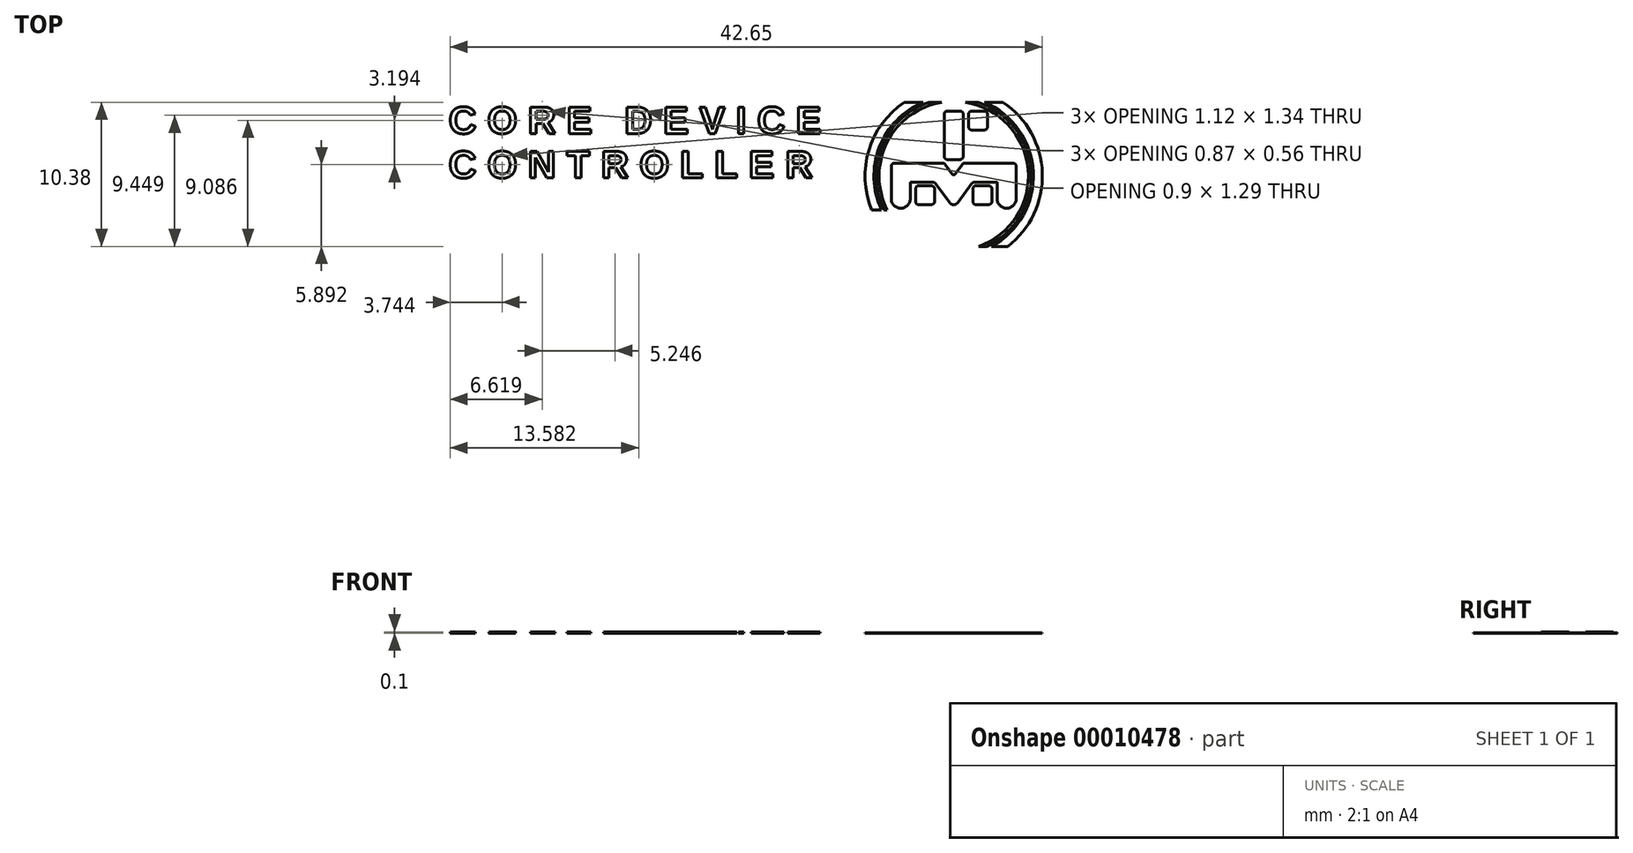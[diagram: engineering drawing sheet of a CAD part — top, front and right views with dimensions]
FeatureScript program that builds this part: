
annotation { "Feature Type Name" : "Feature", "Feature Type Description" : "" }
export const myFeature = defineFeature(function(context is Context, id is Id, definition is map)
    precondition{}
    {
        {
            var Q0;
            Q0=qCreatedBy(makeId("Top.planeOp"),FACE);
            var sketch = newSketch(context, id + "F0", { "sketchPlane" : qUnion([Q0])});
            skLineSegment(sketch, "E0.bottom", {"start": v(62.75, -5.5) * mm, "end": v(66.25, -5.5) * mm});
            skLineSegment(sketch, "E0.top", {"start": v(62.75, -19.5) * mm, "end": v(66.25, -19.5) * mm});
            skLineSegment(sketch, "E0.left", {"start": v(61.75, -6.5) * mm, "end": v(61.75, -18.5) * mm});
            skLineSegment(sketch, "E0.right", {"start": v(67.25, -6.5) * mm, "end": v(67.25, -18.5) * mm});
            skLineSegment(sketch, "E1.bottom", {"start": v(69.75, -5.5) * mm, "end": v(73.25, -5.5) * mm});
            skLineSegment(sketch, "E1.top", {"start": v(69.75, -11) * mm, "end": v(73.25, -11) * mm});
            skLineSegment(sketch, "E1.left", {"start": v(68.75, -6.5) * mm, "end": v(68.75, -10) * mm});
            skLineSegment(sketch, "E1.right", {"start": v(74.25, -6.5) * mm, "end": v(74.25, -10) * mm});
            skLineSegment(sketch, "E2", {"start": v(64.5, -19.5) * mm, "end": v(64.5, -33.5) * mm, "construction": true});
            skLineSegment(sketch, "E3", {"start": v(63.3, -31.86) * mm, "end": v(59.27, -26.4) * mm});
            skLineSegment(sketch, "E4", {"start": v(58.47, -26) * mm, "end": v(52.1, -26) * mm});
            skLineSegment(sketch, "E5", {"start": v(52, -26.1) * mm, "end": v(52, -30.75) * mm});
            skLineSegment(sketch, "E6.0", {"start": v(46.5, -21.5) * mm, "end": v(46.5, -30.75) * mm});
            skLineSegment(sketch, "E6.1", {"start": v(61.24, -20.5) * mm, "end": v(47.5, -20.5) * mm});
            skLineSegment(sketch, "E6.2", {"start": v(64.1, -23.68) * mm, "end": v(62.05, -20.9) * mm});
            skLineSegment(sketch, "E7", {"start": v(49.25, -33.5) * mm, "end": v(49.25, -33.5) * mm});
            skPoint(sketch, "E8.orphan", {"position": v(52, -33.5) * mm});
            skPoint(sketch, "E9.visualSharp", {"position": v(46.5, -33.5) * mm});
            skArc(sketch, "E9.filletArc", {"start": v(46.5, -30.75) * mm, "mid": v(47.3, -32.7) * mm, "end": v(49.25, -33.5) * mm});
            skArc(sketch, "E10.filletArc", {"start": v(49.25, -33.5) * mm, "mid": v(51.2, -32.7) * mm, "end": v(52, -30.75) * mm});
            skLineSegment(sketch, "E11.right", {"start": v(59, -28) * mm, "end": v(59, -31.5) * mm});
            skLineSegment(sketch, "E11.left", {"start": v(53.5, -28) * mm, "end": v(53.5, -31.5) * mm});
            skLineSegment(sketch, "E11.top", {"start": v(54.5, -32.5) * mm, "end": v(58, -32.5) * mm});
            skLineSegment(sketch, "E11.bottom", {"start": v(54.5, -27) * mm, "end": v(58, -27) * mm});
            skPoint(sketch, "E12.0.MirrorP", {"position": v(77, -33.5) * mm});
            skLineSegment(sketch, "E12.1.MirrorCS", {"start": v(74.5, -27) * mm, "end": v(71, -27) * mm});
            skPoint(sketch, "E12.2.MirrorP", {"position": v(82.5, -33.5) * mm});
            skLineSegment(sketch, "E12.3.MirrorCS", {"start": v(70, -28) * mm, "end": v(70, -31.5) * mm});
            skLineSegment(sketch, "E12.4.MirrorCS", {"start": v(75.5, -28) * mm, "end": v(75.5, -31.5) * mm});
            skLineSegment(sketch, "E12.5.MirrorCS", {"start": v(74.5, -32.5) * mm, "end": v(71, -32.5) * mm});
            skLineSegment(sketch, "E12.6.MirrorCS", {"start": v(70.53, -26) * mm, "end": v(76.9, -26) * mm});
            skLineSegment(sketch, "E12.7.MirrorCS", {"start": v(77, -26.1) * mm, "end": v(77, -30.75) * mm});
            skArc(sketch, "E12.8.MirrorCS", {"start": v(79.75, -33.5) * mm, "mid": v(77.8, -32.7) * mm, "end": v(77, -30.75) * mm});
            skLineSegment(sketch, "E12.9.MirrorCS", {"start": v(79.75, -33.5) * mm, "end": v(79.75, -33.5) * mm});
            skLineSegment(sketch, "E12.10.MirrorCS", {"start": v(67.76, -20.5) * mm, "end": v(81.5, -20.5) * mm});
            skPoint(sketch, "E12.11.MirrorP", {"position": v(77, -33.5) * mm});
            skLineSegment(sketch, "E12.12.MirrorCS", {"start": v(64.9, -23.68) * mm, "end": v(66.95, -20.9) * mm});
            skArc(sketch, "E12.13.MirrorCS", {"start": v(82.5, -30.75) * mm, "mid": v(81.7, -32.7) * mm, "end": v(79.75, -33.5) * mm});
            skLineSegment(sketch, "E12.14.MirrorCS", {"start": v(65.7, -31.86) * mm, "end": v(69.73, -26.4) * mm});
            skLineSegment(sketch, "E12.15.MirrorCS", {"start": v(82.5, -21.5) * mm, "end": v(82.5, -30.75) * mm});
            skPoint(sketch, "E13.visualSharp", {"position": v(68.75, -5.5) * mm});
            skArc(sketch, "E13.filletArc", {"start": v(69.75, -5.5) * mm, "mid": v(69.04, -5.8) * mm, "end": v(68.75, -6.5) * mm});
            skPoint(sketch, "E14.visualSharp", {"position": v(74.25, -5.5) * mm});
            skArc(sketch, "E14.filletArc", {"start": v(74.25, -6.5) * mm, "mid": v(73.96, -5.8) * mm, "end": v(73.25, -5.5) * mm});
            skPoint(sketch, "E15.visualSharp", {"position": v(74.25, -11) * mm});
            skArc(sketch, "E15.filletArc", {"start": v(73.25, -11) * mm, "mid": v(73.96, -10.7) * mm, "end": v(74.25, -10) * mm});
            skPoint(sketch, "E16.visualSharp", {"position": v(68.75, -11) * mm});
            skArc(sketch, "E16.filletArc", {"start": v(68.75, -10) * mm, "mid": v(69.04, -10.7) * mm, "end": v(69.75, -11) * mm});
            skPoint(sketch, "E17.visualSharp", {"position": v(67.25, -5.5) * mm});
            skArc(sketch, "E17.filletArc", {"start": v(67.25, -6.5) * mm, "mid": v(66.96, -5.8) * mm, "end": v(66.25, -5.5) * mm});
            skPoint(sketch, "E18.visualSharp", {"position": v(61.75, -5.5) * mm});
            skArc(sketch, "E18.filletArc", {"start": v(62.75, -5.5) * mm, "mid": v(62.04, -5.8) * mm, "end": v(61.75, -6.5) * mm});
            skPoint(sketch, "E19.visualSharp", {"position": v(61.75, -19.5) * mm});
            skArc(sketch, "E19.filletArc", {"start": v(61.75, -18.5) * mm, "mid": v(62.04, -19.2) * mm, "end": v(62.75, -19.5) * mm});
            skPoint(sketch, "E20.visualSharp", {"position": v(67.25, -19.5) * mm});
            skArc(sketch, "E20.filletArc", {"start": v(66.25, -19.5) * mm, "mid": v(66.96, -19.2) * mm, "end": v(67.25, -18.5) * mm});
            skPoint(sketch, "E21.visualSharp", {"position": v(70, -32.5) * mm});
            skArc(sketch, "E21.filletArc", {"start": v(70, -31.5) * mm, "mid": v(70.3, -32.2) * mm, "end": v(71, -32.5) * mm});
            skPoint(sketch, "E22.visualSharp", {"position": v(75.5, -27) * mm});
            skArc(sketch, "E22.filletArc", {"start": v(75.5, -28) * mm, "mid": v(75.2, -27.3) * mm, "end": v(74.5, -27) * mm});
            skPoint(sketch, "E23.visualSharp", {"position": v(70, -27) * mm});
            skArc(sketch, "E23.filletArc", {"start": v(71, -27) * mm, "mid": v(70.3, -27.3) * mm, "end": v(70, -28) * mm});
            skPoint(sketch, "E24.visualSharp", {"position": v(75.5, -32.5) * mm});
            skArc(sketch, "E24.filletArc", {"start": v(74.5, -32.5) * mm, "mid": v(75.2, -32.2) * mm, "end": v(75.5, -31.5) * mm});
            skPoint(sketch, "E25.visualSharp", {"position": v(59, -32.5) * mm});
            skArc(sketch, "E25.filletArc", {"start": v(58, -32.5) * mm, "mid": v(58.7, -32.2) * mm, "end": v(59, -31.5) * mm});
            skPoint(sketch, "E26.visualSharp", {"position": v(59, -27) * mm});
            skArc(sketch, "E26.filletArc", {"start": v(59, -28) * mm, "mid": v(58.7, -27.3) * mm, "end": v(58, -27) * mm});
            skPoint(sketch, "E27.visualSharp", {"position": v(53.5, -27) * mm});
            skArc(sketch, "E27.filletArc", {"start": v(54.5, -27) * mm, "mid": v(53.8, -27.3) * mm, "end": v(53.5, -28) * mm});
            skPoint(sketch, "E28.visualSharp", {"position": v(53.5, -32.5) * mm});
            skArc(sketch, "E28.filletArc", {"start": v(53.5, -31.5) * mm, "mid": v(53.8, -32.2) * mm, "end": v(54.5, -32.5) * mm});
            skPoint(sketch, "E29.visualSharp", {"position": v(46.5, -20.5) * mm});
            skArc(sketch, "E29.filletArc", {"start": v(47.5, -20.5) * mm, "mid": v(46.8, -20.8) * mm, "end": v(46.5, -21.5) * mm});
            skPoint(sketch, "E30.visualSharp", {"position": v(82.5, -20.5) * mm});
            skArc(sketch, "E30.filletArc", {"start": v(82.5, -21.5) * mm, "mid": v(82.2, -20.8) * mm, "end": v(81.5, -20.5) * mm});
            skPoint(sketch, "E31.visualSharp", {"position": v(61.75, -20.5) * mm});
            skArc(sketch, "E31.filletArc", {"start": v(62.05, -20.9) * mm, "mid": v(61.7, -20.6) * mm, "end": v(61.24, -20.5) * mm});
            skPoint(sketch, "E32.visualSharp", {"position": v(67.25, -20.5) * mm});
            skArc(sketch, "E32.filletArc", {"start": v(67.76, -20.5) * mm, "mid": v(67.3, -20.6) * mm, "end": v(66.95, -20.9) * mm});
            skPoint(sketch, "E33.visualSharp", {"position": v(52, -26) * mm});
            skArc(sketch, "E33.filletArc", {"start": v(52.1, -26) * mm, "mid": v(52.03, -26.03) * mm, "end": v(52, -26.1) * mm});
            skPoint(sketch, "E34.visualSharp", {"position": v(77, -26) * mm});
            skArc(sketch, "E34.filletArc", {"start": v(77, -26.1) * mm, "mid": v(76.97, -26.03) * mm, "end": v(76.9, -26) * mm});
            skPoint(sketch, "E35.visualSharp", {"position": v(70.03, -26) * mm});
            skArc(sketch, "E35.filletArc", {"start": v(70.53, -26) * mm, "mid": v(70.08, -26.1) * mm, "end": v(69.73, -26.4) * mm});
            skPoint(sketch, "E36.visualSharp", {"position": v(58.97, -26) * mm});
            skArc(sketch, "E36.filletArc", {"start": v(59.27, -26.4) * mm, "mid": v(58.92, -26.1) * mm, "end": v(58.47, -26) * mm});
            skPoint(sketch, "E37.visualSharp", {"position": v(64.5, -33.5) * mm});
            skArc(sketch, "E37.filletArc", {"start": v(63.3, -31.86) * mm, "mid": v(64.5, -32.47) * mm, "end": v(65.7, -31.86) * mm});
            skPoint(sketch, "E38.visualSharp", {"position": v(64.5, -24.23) * mm});
            skArc(sketch, "E38.filletArc", {"start": v(64.1, -23.68) * mm, "mid": v(64.5, -23.89) * mm, "end": v(64.9, -23.68) * mm});
            skArc(sketch, "E39", {"start": v(71.68, -44.5) * mm, "mid": v(85.92, -22.29) * mm, "end": v(67.92, -3) * mm});
            skArc(sketch, "E40", {"start": v(74, -44.5) * mm, "mid": v(86.85, -22.94) * mm, "end": v(71.6, -3) * mm});
            skArc(sketch, "E41", {"start": v(75.35, -44.5) * mm, "mid": v(87.46, -23.1) * mm, "end": v(73.32, -3) * mm});
            skArc(sketch, "E42", {"start": v(80.06, -44.5) * mm, "mid": v(90.04, -23.4) * mm, "end": v(78.72, -3) * mm});
            skLineSegment(sketch, "E43", {"start": v(80.06, -44.5) * mm, "end": v(75.35, -44.5) * mm});
            skLineSegment(sketch, "E44.trimOffspring", {"start": v(74, -44.5) * mm, "end": v(71.68, -44.5) * mm});
            skLineSegment(sketch, "E45", {"start": v(40.9, -34) * mm, "end": v(43.69, -34) * mm});
            skLineSegment(sketch, "E46.trimOffspring", {"start": v(44.36, -34) * mm, "end": v(45.34, -34) * mm});
            skLineSegment(sketch, "E47", {"start": v(50.28, -3) * mm, "end": v(55.68, -3) * mm});
            skArc(sketch, "E48.trimOffspring", {"start": v(61.08, -3) * mm, "mid": v(45.33, -14.5) * mm, "end": v(45.34, -34) * mm});
            skArc(sketch, "E49.trimOffspring", {"start": v(50.28, -3) * mm, "mid": v(40.05, -16.82) * mm, "end": v(40.9, -34) * mm});
            skArc(sketch, "E50.trimOffspring", {"start": v(55.68, -3) * mm, "mid": v(43.06, -15.94) * mm, "end": v(43.69, -34) * mm});
            skArc(sketch, "E51.trimOffspring", {"start": v(57.4, -3) * mm, "mid": v(43.86, -15.55) * mm, "end": v(44.36, -34) * mm});
            skLineSegment(sketch, "E52.trimOffspring", {"start": v(67.92, -3) * mm, "end": v(71.6, -3) * mm});
            skLineSegment(sketch, "E53.trimOffspring", {"start": v(57.4, -3) * mm, "end": v(61.08, -3) * mm});
            skLineSegment(sketch, "E54.trimOffspring", {"start": v(73.32, -3) * mm, "end": v(78.72, -3) * mm});
            skSolve(sketch);
        }
        {
            var Q0;
            Q0=makeQuery(id+"F0.imprint","IMPRINT",FACE,{"disambiguationData":[TD([[makeQuery(id+"F0.imprint","IMPRINT",EDGE,{"derivedFrom":sQuery(id+"F0.wireOp",EDGE,"46c11c21-c6ca-42b8-9659-15b4f280ee3c.sketch_text.stroke-197")}),1.0]])]});
            var Q1;
            Q1=makeQuery(id+"F0.imprint","IMPRINT",FACE,{"disambiguationData":[TD([[makeQuery(id+"F0.imprint","IMPRINT",EDGE,{"derivedFrom":sQuery(id+"F0.wireOp",EDGE,"E1.bottom")}),-1.0]])]});
            var Q2;
            Q2=makeQuery(id+"F0.imprint","IMPRINT",FACE,{"disambiguationData":[TD([[makeQuery(id+"F0.imprint","IMPRINT",EDGE,{"derivedFrom":sQuery(id+"F0.wireOp",EDGE,"46c11c21-c6ca-42b8-9659-15b4f280ee3c.sketch_text.stroke-126")}),-1.0]])]});
            var Q3;
            Q3=makeQuery(id+"F0.imprint","IMPRINT",FACE,{"disambiguationData":[TD([[makeQuery(id+"F0.imprint","IMPRINT",EDGE,{"derivedFrom":sQuery(id+"F0.wireOp",EDGE,"46c11c21-c6ca-42b8-9659-15b4f280ee3c.sketch_text.stroke-360")}),-1.0]])]});
            var Q4;
            Q4=makeQuery(id+"F0.imprint","IMPRINT",FACE,{"disambiguationData":[TD([[makeQuery(id+"F0.imprint","IMPRINT",EDGE,{"derivedFrom":sQuery(id+"F0.wireOp",EDGE,"E0.bottom")}),-1.0]])]});
            var Q5;
            Q5=makeQuery(id+"F0.imprint","IMPRINT",FACE,{"disambiguationData":[TD([[makeQuery(id+"F0.imprint","IMPRINT",EDGE,{"derivedFrom":sQuery(id+"F0.wireOp",EDGE,"46c11c21-c6ca-42b8-9659-15b4f280ee3c.sketch_text.stroke-0")}),-1.0]])]});
            var Q6;
            Q6=makeQuery(id+"F0.imprint","IMPRINT",FACE,{"disambiguationData":[TD([[makeQuery(id+"F0.imprint","IMPRINT",EDGE,{"derivedFrom":sQuery(id+"F0.wireOp",EDGE,"46c11c21-c6ca-42b8-9659-15b4f280ee3c.sketch_text.stroke-90")}),-1.0]])]});
            var Q7;
            Q7=makeQuery(id+"F0.imprint","IMPRINT",FACE,{"disambiguationData":[TD([[makeQuery(id+"F0.imprint","IMPRINT",EDGE,{"derivedFrom":sQuery(id+"F0.wireOp",EDGE,"46c11c21-c6ca-42b8-9659-15b4f280ee3c.sketch_text.stroke-145")}),-1.0]])]});
            var Q8;
            Q8=makeQuery(id+"F0.imprint","IMPRINT",FACE,{"disambiguationData":[TD([[makeQuery(id+"F0.imprint","IMPRINT",EDGE,{"derivedFrom":sQuery(id+"F0.wireOp",EDGE,"46c11c21-c6ca-42b8-9659-15b4f280ee3c.sketch_text.stroke-126")}),1.0]])]});
            var Q9;
            Q9=makeQuery(id+"F0.imprint","IMPRINT",FACE,{"disambiguationData":[TD([[makeQuery(id+"F0.imprint","IMPRINT",EDGE,{"derivedFrom":sQuery(id+"F0.wireOp",EDGE,"46c11c21-c6ca-42b8-9659-15b4f280ee3c.sketch_text.stroke-48")}),-1.0]])]});
            var Q10;
            Q10=makeQuery(id+"F0.imprint","IMPRINT",FACE,{"disambiguationData":[TD([[makeQuery(id+"F0.imprint","IMPRINT",EDGE,{"derivedFrom":sQuery(id+"F0.wireOp",EDGE,"46c11c21-c6ca-42b8-9659-15b4f280ee3c.sketch_text.stroke-239")}),1.0]])]});
            var Q11;
            Q11=makeQuery(id+"F0.imprint","IMPRINT",FACE,{"disambiguationData":[TD([[makeQuery(id+"F0.imprint","IMPRINT",EDGE,{"derivedFrom":sQuery(id+"F0.wireOp",EDGE,"E12.1.MirrorCS")}),1.0]])]});
            var Q12;
            Q12=makeQuery(id+"F0.imprint","IMPRINT",FACE,{"disambiguationData":[TD([[makeQuery(id+"F0.imprint","IMPRINT",EDGE,{"derivedFrom":sQuery(id+"F0.wireOp",EDGE,"46c11c21-c6ca-42b8-9659-15b4f280ee3c.sketch_text.stroke-300")}),-1.0]])]});
            var Q13;
            Q13=makeQuery(id+"F0.imprint","IMPRINT",FACE,{"disambiguationData":[TD([[makeQuery(id+"F0.imprint","IMPRINT",EDGE,{"derivedFrom":sQuery(id+"F0.wireOp",EDGE,"46c11c21-c6ca-42b8-9659-15b4f280ee3c.sketch_text.stroke-245")}),-1.0]])]});
            var Q14;
            Q14=makeQuery(id+"F0.imprint","IMPRINT",FACE,{"disambiguationData":[TD([[makeQuery(id+"F0.imprint","IMPRINT",EDGE,{"derivedFrom":sQuery(id+"F0.wireOp",EDGE,"46c11c21-c6ca-42b8-9659-15b4f280ee3c.sketch_text.stroke-268")}),-1.0]])]});
            var Q15;
            Q15=makeQuery(id+"F0.imprint","IMPRINT",FACE,{"disambiguationData":[TD([[makeQuery(id+"F0.imprint","IMPRINT",EDGE,{"derivedFrom":sQuery(id+"F0.wireOp",EDGE,"46c11c21-c6ca-42b8-9659-15b4f280ee3c.sketch_text.stroke-189")}),-1.0]])]});
            var Q16;
            Q16=makeQuery(id+"F0.imprint","IMPRINT",FACE,{"disambiguationData":[TD([[makeQuery(id+"F0.imprint","IMPRINT",EDGE,{"derivedFrom":sQuery(id+"F0.wireOp",EDGE,"46c11c21-c6ca-42b8-9659-15b4f280ee3c.sketch_text.stroke-114")}),-1.0]])]});
            var Q17;
            Q17=makeQuery(id+"F0.imprint","IMPRINT",FACE,{"disambiguationData":[TD([[makeQuery(id+"F0.imprint","IMPRINT",EDGE,{"derivedFrom":sQuery(id+"F0.wireOp",EDGE,"E3")}),-1.0]])]});
            var Q18;
            Q18=makeQuery(id+"F0.imprint","IMPRINT",FACE,{"disambiguationData":[TD([[makeQuery(id+"F0.imprint","IMPRINT",EDGE,{"derivedFrom":sQuery(id+"F0.wireOp",EDGE,"46c11c21-c6ca-42b8-9659-15b4f280ee3c.sketch_text.stroke-345")}),-1.0]])]});
            var Q19;
            Q19=makeQuery(id+"F0.imprint","IMPRINT",FACE,{"disambiguationData":[TD([[makeQuery(id+"F0.imprint","IMPRINT",EDGE,{"derivedFrom":sQuery(id+"F0.wireOp",EDGE,"46c11c21-c6ca-42b8-9659-15b4f280ee3c.sketch_text.stroke-232")}),1.0]])]});
            var Q20;
            Q20=makeQuery(id+"F0.imprint","IMPRINT",FACE,{"disambiguationData":[TD([[makeQuery(id+"F0.imprint","IMPRINT",EDGE,{"derivedFrom":sQuery(id+"F0.wireOp",EDGE,"46c11c21-c6ca-42b8-9659-15b4f280ee3c.sketch_text.stroke-280")}),1.0]])]});
            var Q21;
            Q21=makeQuery(id+"F0.imprint","IMPRINT",FACE,{"disambiguationData":[TD([[makeQuery(id+"F0.imprint","IMPRINT",EDGE,{"derivedFrom":sQuery(id+"F0.wireOp",EDGE,"46c11c21-c6ca-42b8-9659-15b4f280ee3c.sketch_text.stroke-161")}),-1.0]])]});
            var Q22;
            Q22=makeQuery(id+"F0.imprint","IMPRINT",FACE,{"disambiguationData":[TD([[makeQuery(id+"F0.imprint","IMPRINT",EDGE,{"derivedFrom":sQuery(id+"F0.wireOp",EDGE,"46c11c21-c6ca-42b8-9659-15b4f280ee3c.sketch_text.stroke-157")}),-1.0]])]});
            var Q23;
            Q23=makeQuery(id+"F0.imprint","IMPRINT",FACE,{"disambiguationData":[TD([[makeQuery(id+"F0.imprint","IMPRINT",EDGE,{"derivedFrom":sQuery(id+"F0.wireOp",EDGE,"46c11c21-c6ca-42b8-9659-15b4f280ee3c.sketch_text.stroke-84")}),1.0]])]});
            var Q24;
            Q24=makeQuery(id+"F0.imprint","IMPRINT",FACE,{"disambiguationData":[TD([[makeQuery(id+"F0.imprint","IMPRINT",EDGE,{"derivedFrom":sQuery(id+"F0.wireOp",EDGE,"46c11c21-c6ca-42b8-9659-15b4f280ee3c.sketch_text.stroke-60")}),-1.0]])]});
            var Q25;
            Q25=makeQuery(id+"F0.imprint","IMPRINT",FACE,{"disambiguationData":[TD([[makeQuery(id+"F0.imprint","IMPRINT",EDGE,{"derivedFrom":sQuery(id+"F0.wireOp",EDGE,"46c11c21-c6ca-42b8-9659-15b4f280ee3c.sketch_text.stroke-340")}),1.0]])]});
            var Q26;
            Q26=makeQuery(id+"F0.imprint","IMPRINT",FACE,{"disambiguationData":[TD([[makeQuery(id+"F0.imprint","IMPRINT",EDGE,{"derivedFrom":sQuery(id+"F0.wireOp",EDGE,"46c11c21-c6ca-42b8-9659-15b4f280ee3c.sketch_text.stroke-220")}),-1.0]])]});
            var Q27;
            Q27=makeQuery(id+"F0.imprint","IMPRINT",FACE,{"disambiguationData":[TD([[makeQuery(id+"F0.imprint","IMPRINT",EDGE,{"derivedFrom":sQuery(id+"F0.wireOp",EDGE,"46c11c21-c6ca-42b8-9659-15b4f280ee3c.sketch_text.stroke-76")}),-1.0]])]});
            var Q28;
            Q28=makeQuery(id+"F0.imprint","IMPRINT",FACE,{"disambiguationData":[TD([[makeQuery(id+"F0.imprint","IMPRINT",EDGE,{"derivedFrom":sQuery(id+"F0.wireOp",EDGE,"46c11c21-c6ca-42b8-9659-15b4f280ee3c.sketch_text.stroke-327")}),1.0]])]});
            var Q29;
            Q29=makeQuery(id+"F0.imprint","IMPRINT",FACE,{"disambiguationData":[TD([[makeQuery(id+"F0.imprint","IMPRINT",EDGE,{"derivedFrom":sQuery(id+"F0.wireOp",EDGE,"46c11c21-c6ca-42b8-9659-15b4f280ee3c.sketch_text.stroke-29")}),-1.0]])]});
            var Q30;
            Q30=makeQuery(id+"F0.imprint","IMPRINT",FACE,{"disambiguationData":[TD([[makeQuery(id+"F0.imprint","IMPRINT",EDGE,{"derivedFrom":sQuery(id+"F0.wireOp",EDGE,"46c11c21-c6ca-42b8-9659-15b4f280ee3c.sketch_text.stroke-60")}),1.0]])]});
            var Q31;
            Q31=makeQuery(id+"F0.imprint","IMPRINT",FACE,{"disambiguationData":[TD([[makeQuery(id+"F0.imprint","IMPRINT",EDGE,{"derivedFrom":sQuery(id+"F0.wireOp",EDGE,"46c11c21-c6ca-42b8-9659-15b4f280ee3c.sketch_text.stroke-333")}),-1.0]])]});
            var Q32;
            Q32=makeQuery(id+"F0.imprint","IMPRINT",FACE,{"disambiguationData":[TD([[makeQuery(id+"F0.imprint","IMPRINT",EDGE,{"derivedFrom":sQuery(id+"F0.wireOp",EDGE,"E11.right")}),-1.0]])]});
            var Q33;
            Q33=makeQuery(id+"F0.imprint","IMPRINT",FACE,{"disambiguationData":[TD([[makeQuery(id+"F0.imprint","IMPRINT",EDGE,{"derivedFrom":sQuery(id+"F0.wireOp",EDGE,"46c11c21-c6ca-42b8-9659-15b4f280ee3c.sketch_text.stroke-216")}),-1.0]])]});
            var Q34;
            Q34=makeQuery(id+"F0.imprint","IMPRINT",FACE,{"disambiguationData":[TD([[makeQuery(id+"F0.imprint","IMPRINT",EDGE,{"derivedFrom":sQuery(id+"F0.wireOp",EDGE,"46c11c21-c6ca-42b8-9659-15b4f280ee3c.sketch_text.stroke-260")}),-1.0]])]});
            var Q35;
            Q35=makeQuery(id+"F0.imprint","IMPRINT",FACE,{"disambiguationData":[TD([[makeQuery(id+"F0.imprint","IMPRINT",EDGE,{"derivedFrom":sQuery(id+"F0.wireOp",EDGE,"46c11c21-c6ca-42b8-9659-15b4f280ee3c.sketch_text.stroke-286")}),-1.0]])]});
            var Q36;
            Q36=makeQuery(id+"F0.imprint","IMPRINT",FACE,{"disambiguationData":[TD([[makeQuery(id+"F0.imprint","IMPRINT",EDGE,{"derivedFrom":sQuery(id+"F0.wireOp",EDGE,"46c11c21-c6ca-42b8-9659-15b4f280ee3c.sketch_text.stroke-197")}),-1.0]])]});
            var Q37;
            Q37=makeQuery(id+"F0.imprint","IMPRINT",FACE,{"disambiguationData":[TD([[makeQuery(id+"F0.imprint","IMPRINT",EDGE,{"derivedFrom":sQuery(id+"F0.wireOp",EDGE,"46c11c21-c6ca-42b8-9659-15b4f280ee3c.sketch_text.stroke-319")}),-1.0]])]});
            var Q38;
            Q38=makeQuery(id+"F0.imprint","IMPRINT",FACE,{"disambiguationData":[TD([[makeQuery(id+"F0.imprint","IMPRINT",EDGE,{"derivedFrom":sQuery(id+"F0.wireOp",EDGE,"46c11c21-c6ca-42b8-9659-15b4f280ee3c.sketch_text.stroke-366")}),-1.0]])]});
            var Q39;
            Q39=makeQuery(id+"F0.imprint","IMPRINT",FACE,{"disambiguationData":[TD([[makeQuery(id+"F0.imprint","IMPRINT",EDGE,{"derivedFrom":sQuery(id+"F0.wireOp",EDGE,"46c11c21-c6ca-42b8-9659-15b4f280ee3c.sketch_text.stroke-272")}),-1.0]])]});
            var Q40;
            Q40=makeQuery(id+"F0.imprint","IMPRINT",FACE,{"disambiguationData":[TD([[makeQuery(id+"F0.imprint","IMPRINT",EDGE,{"derivedFrom":sQuery(id+"F0.wireOp",EDGE,"46c11c21-c6ca-42b8-9659-15b4f280ee3c.sketch_text.stroke-15")}),-1.0]])]});
            var Q41;
            Q41=makeQuery(id+"F0.imprint","IMPRINT",FACE,{"disambiguationData":[TD([[makeQuery(id+"F0.imprint","IMPRINT",EDGE,{"derivedFrom":sQuery(id+"F0.wireOp",EDGE,"46c11c21-c6ca-42b8-9659-15b4f280ee3c.sketch_text.stroke-168")}),-1.0]])]});
            var Q42;
            Q42=makeQuery(id+"F0.imprint","IMPRINT",FACE,{"disambiguationData":[TD([[makeQuery(id+"F0.imprint","IMPRINT",EDGE,{"derivedFrom":sQuery(id+"F0.wireOp",EDGE,"46c11c21-c6ca-42b8-9659-15b4f280ee3c.sketch_text.stroke-95")}),-1.0]])]});
            var Q43;
            Q43=makeQuery(id+"F0.imprint","IMPRINT",FACE,{"disambiguationData":[TD([[makeQuery(id+"F0.imprint","IMPRINT",EDGE,{"derivedFrom":sQuery(id+"F0.wireOp",EDGE,"46c11c21-c6ca-42b8-9659-15b4f280ee3c.sketch_text.stroke-225")}),-1.0]])]});
            var Q44;
            Q44=makeQuery(id+"F0.imprint","IMPRINT",FACE,{"disambiguationData":[TD([[makeQuery(id+"F0.imprint","IMPRINT",EDGE,{"derivedFrom":sQuery(id+"F0.wireOp",EDGE,"46c11c21-c6ca-42b8-9659-15b4f280ee3c.sketch_text.stroke-231")}),-1.0]])]});
            var Q45;
            Q45=makeQuery(id+"F0.imprint","IMPRINT",FACE,{"disambiguationData":[TD([[makeQuery(id+"F0.imprint","IMPRINT",EDGE,{"derivedFrom":sQuery(id+"F0.wireOp",EDGE,"46c11c21-c6ca-42b8-9659-15b4f280ee3c.sketch_text.stroke-177")}),-1.0]])]});
            var Q46;
            Q46=makeQuery(id+"F0.imprint","IMPRINT",FACE,{"disambiguationData":[TD([[makeQuery(id+"F0.imprint","IMPRINT",EDGE,{"derivedFrom":sQuery(id+"F0.wireOp",EDGE,"E41")}),-1.0]])]});
            var Q47;
            Q47=makeQuery(id+"F0.imprint","IMPRINT",FACE,{"disambiguationData":[TD([[makeQuery(id+"F0.imprint","IMPRINT",EDGE,{"derivedFrom":sQuery(id+"F0.wireOp",EDGE,"E39")}),-1.0]])]});
            var Q48;
            Q48=makeQuery(id+"F0.imprint","IMPRINT",FACE,{"disambiguationData":[TD([[makeQuery(id+"F0.imprint","IMPRINT",EDGE,{"derivedFrom":sQuery(id+"F0.wireOp",EDGE,"E45")}),1.0]])]});
            var Q49;
            Q49=makeQuery(id+"F0.imprint","IMPRINT",FACE,{"disambiguationData":[TD([[makeQuery(id+"F0.imprint","IMPRINT",EDGE,{"derivedFrom":sQuery(id+"F0.wireOp",EDGE,"E46.trimOffspring")}),1.0]])]});
            extrude(context, id + "F1", {"entities" : qUnion([Q0, Q1, Q2, Q3, Q4, Q5, Q6, Q7, Q8, Q9, Q10, Q11, Q12, Q13, Q14, Q15, Q16, Q17, Q18, Q19, Q20, Q21, Q22, Q23, Q24, Q25, Q26, Q27, Q28, Q29, Q30, Q31, Q32, Q33, Q34, Q35, Q36, Q37, Q38, Q39, Q40, Q41, Q42, Q43, Q44, Q45, Q46, Q47, Q48, Q49]), "depth" : .1 * mm});
        }
        {
            var Q0;
            Q0=makeQuery(id+"F1.opExtrude","SWEPT_BODY",BODY,{"disambiguationData":[OSD([sQuery(id+"F0.wireOp",EDGE,"46c11c21-c6ca-42b8-9659-15b4f280ee3c.sketch_text.stroke-149"),sQuery(id+"F0.wireOp",EDGE,"46c11c21-c6ca-42b8-9659-15b4f280ee3c.sketch_text.stroke-150"),sQuery(id+"F0.wireOp",EDGE,"46c11c21-c6ca-42b8-9659-15b4f280ee3c.sketch_text.stroke-151"),sQuery(id+"F0.wireOp",EDGE,"46c11c21-c6ca-42b8-9659-15b4f280ee3c.sketch_text.stroke-152"),sQuery(id+"F0.wireOp",EDGE,"46c11c21-c6ca-42b8-9659-15b4f280ee3c.sketch_text.stroke-153"),sQuery(id+"F0.wireOp",EDGE,"46c11c21-c6ca-42b8-9659-15b4f280ee3c.sketch_text.stroke-154"),sQuery(id+"F0.wireOp",EDGE,"46c11c21-c6ca-42b8-9659-15b4f280ee3c.sketch_text.stroke-155"),sQuery(id+"F0.wireOp",EDGE,"46c11c21-c6ca-42b8-9659-15b4f280ee3c.sketch_text.stroke-156"),sQuery(id+"F0.wireOp",EDGE,"46c11c21-c6ca-42b8-9659-15b4f280ee3c.sketch_text.stroke-157"),sQuery(id+"F0.wireOp",EDGE,"46c11c21-c6ca-42b8-9659-15b4f280ee3c.sketch_text.stroke-158"),sQuery(id+"F0.wireOp",EDGE,"46c11c21-c6ca-42b8-9659-15b4f280ee3c.sketch_text.stroke-159"),sQuery(id+"F0.wireOp",EDGE,"46c11c21-c6ca-42b8-9659-15b4f280ee3c.sketch_text.stroke-160"),sQuery(id+"F0.wireOp",EDGE,"46c11c21-c6ca-42b8-9659-15b4f280ee3c.sketch_text.stroke-161"),sQuery(id+"F0.wireOp",EDGE,"46c11c21-c6ca-42b8-9659-15b4f280ee3c.sketch_text.stroke-162")])]});
            var Q1;
            Q1=makeQuery(id+"F1.opExtrude","SWEPT_BODY",BODY,{"disambiguationData":[OSD([sQuery(id+"F0.wireOp",EDGE,"46c11c21-c6ca-42b8-9659-15b4f280ee3c.sketch_text.stroke-134"),sQuery(id+"F0.wireOp",EDGE,"46c11c21-c6ca-42b8-9659-15b4f280ee3c.sketch_text.stroke-135"),sQuery(id+"F0.wireOp",EDGE,"46c11c21-c6ca-42b8-9659-15b4f280ee3c.sketch_text.stroke-136"),sQuery(id+"F0.wireOp",EDGE,"46c11c21-c6ca-42b8-9659-15b4f280ee3c.sketch_text.stroke-137"),sQuery(id+"F0.wireOp",EDGE,"46c11c21-c6ca-42b8-9659-15b4f280ee3c.sketch_text.stroke-138"),sQuery(id+"F0.wireOp",EDGE,"46c11c21-c6ca-42b8-9659-15b4f280ee3c.sketch_text.stroke-139"),sQuery(id+"F0.wireOp",EDGE,"46c11c21-c6ca-42b8-9659-15b4f280ee3c.sketch_text.stroke-140"),sQuery(id+"F0.wireOp",EDGE,"46c11c21-c6ca-42b8-9659-15b4f280ee3c.sketch_text.stroke-141"),sQuery(id+"F0.wireOp",EDGE,"46c11c21-c6ca-42b8-9659-15b4f280ee3c.sketch_text.stroke-142"),sQuery(id+"F0.wireOp",EDGE,"46c11c21-c6ca-42b8-9659-15b4f280ee3c.sketch_text.stroke-143"),sQuery(id+"F0.wireOp",EDGE,"46c11c21-c6ca-42b8-9659-15b4f280ee3c.sketch_text.stroke-144"),sQuery(id+"F0.wireOp",EDGE,"46c11c21-c6ca-42b8-9659-15b4f280ee3c.sketch_text.stroke-145"),sQuery(id+"F0.wireOp",EDGE,"46c11c21-c6ca-42b8-9659-15b4f280ee3c.sketch_text.stroke-146"),sQuery(id+"F0.wireOp",EDGE,"46c11c21-c6ca-42b8-9659-15b4f280ee3c.sketch_text.stroke-147"),sQuery(id+"F0.wireOp",EDGE,"46c11c21-c6ca-42b8-9659-15b4f280ee3c.sketch_text.stroke-148")])]});
            var Q2;
            Q2=makeQuery(id+"F1.opExtrude","SWEPT_BODY",BODY,{"disambiguationData":[OSD([sQuery(id+"F0.wireOp",EDGE,"46c11c21-c6ca-42b8-9659-15b4f280ee3c.sketch_text.stroke-101"),sQuery(id+"F0.wireOp",EDGE,"46c11c21-c6ca-42b8-9659-15b4f280ee3c.sketch_text.stroke-102"),sQuery(id+"F0.wireOp",EDGE,"46c11c21-c6ca-42b8-9659-15b4f280ee3c.sketch_text.stroke-103"),sQuery(id+"F0.wireOp",EDGE,"46c11c21-c6ca-42b8-9659-15b4f280ee3c.sketch_text.stroke-104"),sQuery(id+"F0.wireOp",EDGE,"46c11c21-c6ca-42b8-9659-15b4f280ee3c.sketch_text.stroke-105"),sQuery(id+"F0.wireOp",EDGE,"46c11c21-c6ca-42b8-9659-15b4f280ee3c.sketch_text.stroke-106"),sQuery(id+"F0.wireOp",EDGE,"46c11c21-c6ca-42b8-9659-15b4f280ee3c.sketch_text.stroke-107"),sQuery(id+"F0.wireOp",EDGE,"46c11c21-c6ca-42b8-9659-15b4f280ee3c.sketch_text.stroke-108"),sQuery(id+"F0.wireOp",EDGE,"46c11c21-c6ca-42b8-9659-15b4f280ee3c.sketch_text.stroke-109"),sQuery(id+"F0.wireOp",EDGE,"46c11c21-c6ca-42b8-9659-15b4f280ee3c.sketch_text.stroke-110"),sQuery(id+"F0.wireOp",EDGE,"46c11c21-c6ca-42b8-9659-15b4f280ee3c.sketch_text.stroke-111"),sQuery(id+"F0.wireOp",EDGE,"46c11c21-c6ca-42b8-9659-15b4f280ee3c.sketch_text.stroke-112"),sQuery(id+"F0.wireOp",EDGE,"46c11c21-c6ca-42b8-9659-15b4f280ee3c.sketch_text.stroke-113"),sQuery(id+"F0.wireOp",EDGE,"46c11c21-c6ca-42b8-9659-15b4f280ee3c.sketch_text.stroke-114")])]});
            var Q3;
            Q3=makeQuery(id+"F1.opExtrude","SWEPT_BODY",BODY,{"disambiguationData":[OSD([sQuery(id+"F0.wireOp",EDGE,"46c11c21-c6ca-42b8-9659-15b4f280ee3c.sketch_text.stroke-79"),sQuery(id+"F0.wireOp",EDGE,"46c11c21-c6ca-42b8-9659-15b4f280ee3c.sketch_text.stroke-80"),sQuery(id+"F0.wireOp",EDGE,"46c11c21-c6ca-42b8-9659-15b4f280ee3c.sketch_text.stroke-81"),sQuery(id+"F0.wireOp",EDGE,"46c11c21-c6ca-42b8-9659-15b4f280ee3c.sketch_text.stroke-82"),sQuery(id+"F0.wireOp",EDGE,"46c11c21-c6ca-42b8-9659-15b4f280ee3c.sketch_text.stroke-83"),sQuery(id+"F0.wireOp",EDGE,"46c11c21-c6ca-42b8-9659-15b4f280ee3c.sketch_text.stroke-84"),sQuery(id+"F0.wireOp",EDGE,"46c11c21-c6ca-42b8-9659-15b4f280ee3c.sketch_text.stroke-85"),sQuery(id+"F0.wireOp",EDGE,"46c11c21-c6ca-42b8-9659-15b4f280ee3c.sketch_text.stroke-86"),sQuery(id+"F0.wireOp",EDGE,"46c11c21-c6ca-42b8-9659-15b4f280ee3c.sketch_text.stroke-87"),sQuery(id+"F0.wireOp",EDGE,"46c11c21-c6ca-42b8-9659-15b4f280ee3c.sketch_text.stroke-88"),sQuery(id+"F0.wireOp",EDGE,"46c11c21-c6ca-42b8-9659-15b4f280ee3c.sketch_text.stroke-89"),sQuery(id+"F0.wireOp",EDGE,"46c11c21-c6ca-42b8-9659-15b4f280ee3c.sketch_text.stroke-90"),sQuery(id+"F0.wireOp",EDGE,"46c11c21-c6ca-42b8-9659-15b4f280ee3c.sketch_text.stroke-91"),sQuery(id+"F0.wireOp",EDGE,"46c11c21-c6ca-42b8-9659-15b4f280ee3c.sketch_text.stroke-92")])]});
            var Q4;
            Q4=makeQuery(id+"F1.opExtrude","SWEPT_BODY",BODY,{"disambiguationData":[OSD([sQuery(id+"F0.wireOp",EDGE,"E0.bottom"),sQuery(id+"F0.wireOp",EDGE,"E0.top"),sQuery(id+"F0.wireOp",EDGE,"E0.left"),sQuery(id+"F0.wireOp",EDGE,"E0.right"),sQuery(id+"F0.wireOp",EDGE,"E17.filletArc"),sQuery(id+"F0.wireOp",EDGE,"E18.filletArc"),sQuery(id+"F0.wireOp",EDGE,"E19.filletArc"),sQuery(id+"F0.wireOp",EDGE,"E20.filletArc")])]});
            var Q5;
            Q5=makeQuery(id+"F1.opExtrude","SWEPT_BODY",BODY,{"disambiguationData":[OSD([sQuery(id+"F0.wireOp",EDGE,"46c11c21-c6ca-42b8-9659-15b4f280ee3c.sketch_text.stroke-242"),sQuery(id+"F0.wireOp",EDGE,"46c11c21-c6ca-42b8-9659-15b4f280ee3c.sketch_text.stroke-243"),sQuery(id+"F0.wireOp",EDGE,"46c11c21-c6ca-42b8-9659-15b4f280ee3c.sketch_text.stroke-244"),sQuery(id+"F0.wireOp",EDGE,"46c11c21-c6ca-42b8-9659-15b4f280ee3c.sketch_text.stroke-245"),sQuery(id+"F0.wireOp",EDGE,"46c11c21-c6ca-42b8-9659-15b4f280ee3c.sketch_text.stroke-246"),sQuery(id+"F0.wireOp",EDGE,"46c11c21-c6ca-42b8-9659-15b4f280ee3c.sketch_text.stroke-247"),sQuery(id+"F0.wireOp",EDGE,"46c11c21-c6ca-42b8-9659-15b4f280ee3c.sketch_text.stroke-248"),sQuery(id+"F0.wireOp",EDGE,"46c11c21-c6ca-42b8-9659-15b4f280ee3c.sketch_text.stroke-249"),sQuery(id+"F0.wireOp",EDGE,"46c11c21-c6ca-42b8-9659-15b4f280ee3c.sketch_text.stroke-250"),sQuery(id+"F0.wireOp",EDGE,"46c11c21-c6ca-42b8-9659-15b4f280ee3c.sketch_text.stroke-251"),sQuery(id+"F0.wireOp",EDGE,"46c11c21-c6ca-42b8-9659-15b4f280ee3c.sketch_text.stroke-252"),sQuery(id+"F0.wireOp",EDGE,"46c11c21-c6ca-42b8-9659-15b4f280ee3c.sketch_text.stroke-253"),sQuery(id+"F0.wireOp",EDGE,"46c11c21-c6ca-42b8-9659-15b4f280ee3c.sketch_text.stroke-254"),sQuery(id+"F0.wireOp",EDGE,"46c11c21-c6ca-42b8-9659-15b4f280ee3c.sketch_text.stroke-255"),sQuery(id+"F0.wireOp",EDGE,"46c11c21-c6ca-42b8-9659-15b4f280ee3c.sketch_text.stroke-256"),sQuery(id+"F0.wireOp",EDGE,"46c11c21-c6ca-42b8-9659-15b4f280ee3c.sketch_text.stroke-257"),sQuery(id+"F0.wireOp",EDGE,"46c11c21-c6ca-42b8-9659-15b4f280ee3c.sketch_text.stroke-258"),sQuery(id+"F0.wireOp",EDGE,"46c11c21-c6ca-42b8-9659-15b4f280ee3c.sketch_text.stroke-259"),sQuery(id+"F0.wireOp",EDGE,"46c11c21-c6ca-42b8-9659-15b4f280ee3c.sketch_text.stroke-260")])]});
            var Q6;
            Q6=makeQuery(id+"F1.opExtrude","SWEPT_BODY",BODY,{"disambiguationData":[OSD([sQuery(id+"F0.wireOp",EDGE,"46c11c21-c6ca-42b8-9659-15b4f280ee3c.sketch_text.stroke-230"),sQuery(id+"F0.wireOp",EDGE,"46c11c21-c6ca-42b8-9659-15b4f280ee3c.sketch_text.stroke-231"),sQuery(id+"F0.wireOp",EDGE,"46c11c21-c6ca-42b8-9659-15b4f280ee3c.sketch_text.stroke-232"),sQuery(id+"F0.wireOp",EDGE,"46c11c21-c6ca-42b8-9659-15b4f280ee3c.sketch_text.stroke-233"),sQuery(id+"F0.wireOp",EDGE,"46c11c21-c6ca-42b8-9659-15b4f280ee3c.sketch_text.stroke-234"),sQuery(id+"F0.wireOp",EDGE,"46c11c21-c6ca-42b8-9659-15b4f280ee3c.sketch_text.stroke-235"),sQuery(id+"F0.wireOp",EDGE,"46c11c21-c6ca-42b8-9659-15b4f280ee3c.sketch_text.stroke-236"),sQuery(id+"F0.wireOp",EDGE,"46c11c21-c6ca-42b8-9659-15b4f280ee3c.sketch_text.stroke-237"),sQuery(id+"F0.wireOp",EDGE,"46c11c21-c6ca-42b8-9659-15b4f280ee3c.sketch_text.stroke-238"),sQuery(id+"F0.wireOp",EDGE,"46c11c21-c6ca-42b8-9659-15b4f280ee3c.sketch_text.stroke-239"),sQuery(id+"F0.wireOp",EDGE,"46c11c21-c6ca-42b8-9659-15b4f280ee3c.sketch_text.stroke-240"),sQuery(id+"F0.wireOp",EDGE,"46c11c21-c6ca-42b8-9659-15b4f280ee3c.sketch_text.stroke-241")])]});
            var Q7;
            Q7=makeQuery(id+"F1.opExtrude","SWEPT_BODY",BODY,{"disambiguationData":[OSD([sQuery(id+"F0.wireOp",EDGE,"46c11c21-c6ca-42b8-9659-15b4f280ee3c.sketch_text.stroke-218"),sQuery(id+"F0.wireOp",EDGE,"46c11c21-c6ca-42b8-9659-15b4f280ee3c.sketch_text.stroke-219"),sQuery(id+"F0.wireOp",EDGE,"46c11c21-c6ca-42b8-9659-15b4f280ee3c.sketch_text.stroke-220"),sQuery(id+"F0.wireOp",EDGE,"46c11c21-c6ca-42b8-9659-15b4f280ee3c.sketch_text.stroke-221"),sQuery(id+"F0.wireOp",EDGE,"46c11c21-c6ca-42b8-9659-15b4f280ee3c.sketch_text.stroke-222"),sQuery(id+"F0.wireOp",EDGE,"46c11c21-c6ca-42b8-9659-15b4f280ee3c.sketch_text.stroke-223")])]});
            var Q8;
            Q8=makeQuery(id+"F1.opExtrude","SWEPT_BODY",BODY,{"disambiguationData":[OSD([sQuery(id+"F0.wireOp",EDGE,"46c11c21-c6ca-42b8-9659-15b4f280ee3c.sketch_text.stroke-204"),sQuery(id+"F0.wireOp",EDGE,"46c11c21-c6ca-42b8-9659-15b4f280ee3c.sketch_text.stroke-205"),sQuery(id+"F0.wireOp",EDGE,"46c11c21-c6ca-42b8-9659-15b4f280ee3c.sketch_text.stroke-206"),sQuery(id+"F0.wireOp",EDGE,"46c11c21-c6ca-42b8-9659-15b4f280ee3c.sketch_text.stroke-207"),sQuery(id+"F0.wireOp",EDGE,"46c11c21-c6ca-42b8-9659-15b4f280ee3c.sketch_text.stroke-208"),sQuery(id+"F0.wireOp",EDGE,"46c11c21-c6ca-42b8-9659-15b4f280ee3c.sketch_text.stroke-209"),sQuery(id+"F0.wireOp",EDGE,"46c11c21-c6ca-42b8-9659-15b4f280ee3c.sketch_text.stroke-210"),sQuery(id+"F0.wireOp",EDGE,"46c11c21-c6ca-42b8-9659-15b4f280ee3c.sketch_text.stroke-211"),sQuery(id+"F0.wireOp",EDGE,"46c11c21-c6ca-42b8-9659-15b4f280ee3c.sketch_text.stroke-212"),sQuery(id+"F0.wireOp",EDGE,"46c11c21-c6ca-42b8-9659-15b4f280ee3c.sketch_text.stroke-213"),sQuery(id+"F0.wireOp",EDGE,"46c11c21-c6ca-42b8-9659-15b4f280ee3c.sketch_text.stroke-214"),sQuery(id+"F0.wireOp",EDGE,"46c11c21-c6ca-42b8-9659-15b4f280ee3c.sketch_text.stroke-215"),sQuery(id+"F0.wireOp",EDGE,"46c11c21-c6ca-42b8-9659-15b4f280ee3c.sketch_text.stroke-216"),sQuery(id+"F0.wireOp",EDGE,"46c11c21-c6ca-42b8-9659-15b4f280ee3c.sketch_text.stroke-217")])]});
            var Q9;
            Q9=makeQuery(id+"F1.opExtrude","SWEPT_BODY",BODY,{"disambiguationData":[OSD([sQuery(id+"F0.wireOp",EDGE,"46c11c21-c6ca-42b8-9659-15b4f280ee3c.sketch_text.stroke-29"),sQuery(id+"F0.wireOp",EDGE,"46c11c21-c6ca-42b8-9659-15b4f280ee3c.sketch_text.stroke-30"),sQuery(id+"F0.wireOp",EDGE,"46c11c21-c6ca-42b8-9659-15b4f280ee3c.sketch_text.stroke-31"),sQuery(id+"F0.wireOp",EDGE,"46c11c21-c6ca-42b8-9659-15b4f280ee3c.sketch_text.stroke-32"),sQuery(id+"F0.wireOp",EDGE,"46c11c21-c6ca-42b8-9659-15b4f280ee3c.sketch_text.stroke-33"),sQuery(id+"F0.wireOp",EDGE,"46c11c21-c6ca-42b8-9659-15b4f280ee3c.sketch_text.stroke-34"),sQuery(id+"F0.wireOp",EDGE,"46c11c21-c6ca-42b8-9659-15b4f280ee3c.sketch_text.stroke-35"),sQuery(id+"F0.wireOp",EDGE,"46c11c21-c6ca-42b8-9659-15b4f280ee3c.sketch_text.stroke-36"),sQuery(id+"F0.wireOp",EDGE,"46c11c21-c6ca-42b8-9659-15b4f280ee3c.sketch_text.stroke-37"),sQuery(id+"F0.wireOp",EDGE,"46c11c21-c6ca-42b8-9659-15b4f280ee3c.sketch_text.stroke-38"),sQuery(id+"F0.wireOp",EDGE,"46c11c21-c6ca-42b8-9659-15b4f280ee3c.sketch_text.stroke-39"),sQuery(id+"F0.wireOp",EDGE,"46c11c21-c6ca-42b8-9659-15b4f280ee3c.sketch_text.stroke-40"),sQuery(id+"F0.wireOp",EDGE,"46c11c21-c6ca-42b8-9659-15b4f280ee3c.sketch_text.stroke-41"),sQuery(id+"F0.wireOp",EDGE,"46c11c21-c6ca-42b8-9659-15b4f280ee3c.sketch_text.stroke-42"),sQuery(id+"F0.wireOp",EDGE,"46c11c21-c6ca-42b8-9659-15b4f280ee3c.sketch_text.stroke-43"),sQuery(id+"F0.wireOp",EDGE,"46c11c21-c6ca-42b8-9659-15b4f280ee3c.sketch_text.stroke-44"),sQuery(id+"F0.wireOp",EDGE,"46c11c21-c6ca-42b8-9659-15b4f280ee3c.sketch_text.stroke-45"),sQuery(id+"F0.wireOp",EDGE,"46c11c21-c6ca-42b8-9659-15b4f280ee3c.sketch_text.stroke-46"),sQuery(id+"F0.wireOp",EDGE,"46c11c21-c6ca-42b8-9659-15b4f280ee3c.sketch_text.stroke-47")])]});
            var Q10;
            Q10=makeQuery(id+"F1.opExtrude","SWEPT_BODY",BODY,{"disambiguationData":[OSD([sQuery(id+"F0.wireOp",EDGE,"46c11c21-c6ca-42b8-9659-15b4f280ee3c.sketch_text.stroke-15"),sQuery(id+"F0.wireOp",EDGE,"46c11c21-c6ca-42b8-9659-15b4f280ee3c.sketch_text.stroke-16"),sQuery(id+"F0.wireOp",EDGE,"46c11c21-c6ca-42b8-9659-15b4f280ee3c.sketch_text.stroke-17"),sQuery(id+"F0.wireOp",EDGE,"46c11c21-c6ca-42b8-9659-15b4f280ee3c.sketch_text.stroke-18"),sQuery(id+"F0.wireOp",EDGE,"46c11c21-c6ca-42b8-9659-15b4f280ee3c.sketch_text.stroke-19"),sQuery(id+"F0.wireOp",EDGE,"46c11c21-c6ca-42b8-9659-15b4f280ee3c.sketch_text.stroke-20"),sQuery(id+"F0.wireOp",EDGE,"46c11c21-c6ca-42b8-9659-15b4f280ee3c.sketch_text.stroke-21"),sQuery(id+"F0.wireOp",EDGE,"46c11c21-c6ca-42b8-9659-15b4f280ee3c.sketch_text.stroke-22"),sQuery(id+"F0.wireOp",EDGE,"46c11c21-c6ca-42b8-9659-15b4f280ee3c.sketch_text.stroke-23"),sQuery(id+"F0.wireOp",EDGE,"46c11c21-c6ca-42b8-9659-15b4f280ee3c.sketch_text.stroke-24"),sQuery(id+"F0.wireOp",EDGE,"46c11c21-c6ca-42b8-9659-15b4f280ee3c.sketch_text.stroke-25"),sQuery(id+"F0.wireOp",EDGE,"46c11c21-c6ca-42b8-9659-15b4f280ee3c.sketch_text.stroke-26"),sQuery(id+"F0.wireOp",EDGE,"46c11c21-c6ca-42b8-9659-15b4f280ee3c.sketch_text.stroke-27"),sQuery(id+"F0.wireOp",EDGE,"46c11c21-c6ca-42b8-9659-15b4f280ee3c.sketch_text.stroke-28")])]});
            var Q11;
            Q11=makeQuery(id+"F1.opExtrude","SWEPT_BODY",BODY,{"disambiguationData":[OSD([sQuery(id+"F0.wireOp",EDGE,"E3"),sQuery(id+"F0.wireOp",EDGE,"E4"),sQuery(id+"F0.wireOp",EDGE,"E5"),sQuery(id+"F0.wireOp",EDGE,"E6.0"),sQuery(id+"F0.wireOp",EDGE,"E6.1"),sQuery(id+"F0.wireOp",EDGE,"E6.2"),sQuery(id+"F0.wireOp",EDGE,"E9.filletArc"),sQuery(id+"F0.wireOp",EDGE,"E10.filletArc"),sQuery(id+"F0.wireOp",EDGE,"E12.6.MirrorCS"),sQuery(id+"F0.wireOp",EDGE,"E12.7.MirrorCS"),sQuery(id+"F0.wireOp",EDGE,"E12.8.MirrorCS"),sQuery(id+"F0.wireOp",EDGE,"E12.10.MirrorCS"),sQuery(id+"F0.wireOp",EDGE,"E12.12.MirrorCS"),sQuery(id+"F0.wireOp",EDGE,"E12.13.MirrorCS"),sQuery(id+"F0.wireOp",EDGE,"E12.14.MirrorCS"),sQuery(id+"F0.wireOp",EDGE,"E12.15.MirrorCS"),sQuery(id+"F0.wireOp",EDGE,"E29.filletArc"),sQuery(id+"F0.wireOp",EDGE,"E30.filletArc"),sQuery(id+"F0.wireOp",EDGE,"E31.filletArc"),sQuery(id+"F0.wireOp",EDGE,"E32.filletArc"),sQuery(id+"F0.wireOp",EDGE,"E33.filletArc"),sQuery(id+"F0.wireOp",EDGE,"E34.filletArc"),sQuery(id+"F0.wireOp",EDGE,"E35.filletArc"),sQuery(id+"F0.wireOp",EDGE,"E36.filletArc"),sQuery(id+"F0.wireOp",EDGE,"E37.filletArc"),sQuery(id+"F0.wireOp",EDGE,"E38.filletArc")])]});
            var Q12;
            Q12=makeQuery(id+"F1.opExtrude","SWEPT_BODY",BODY,{"disambiguationData":[OSD([sQuery(id+"F0.wireOp",EDGE,"E12.1.MirrorCS"),sQuery(id+"F0.wireOp",EDGE,"E12.3.MirrorCS"),sQuery(id+"F0.wireOp",EDGE,"E12.4.MirrorCS"),sQuery(id+"F0.wireOp",EDGE,"E12.5.MirrorCS"),sQuery(id+"F0.wireOp",EDGE,"E21.filletArc"),sQuery(id+"F0.wireOp",EDGE,"E22.filletArc"),sQuery(id+"F0.wireOp",EDGE,"E23.filletArc"),sQuery(id+"F0.wireOp",EDGE,"E24.filletArc")])]});
            var Q13;
            Q13=makeQuery(id+"F1.opExtrude","SWEPT_BODY",BODY,{"disambiguationData":[OSD([sQuery(id+"F0.wireOp",EDGE,"E41"),sQuery(id+"F0.wireOp",EDGE,"E42"),sQuery(id+"F0.wireOp",EDGE,"E43"),sQuery(id+"F0.wireOp",EDGE,"E54.trimOffspring")])]});
            var Q14;
            Q14=makeQuery(id+"F1.opExtrude","SWEPT_BODY",BODY,{"disambiguationData":[OSD([sQuery(id+"F0.wireOp",EDGE,"46c11c21-c6ca-42b8-9659-15b4f280ee3c.sketch_text.stroke-163"),sQuery(id+"F0.wireOp",EDGE,"46c11c21-c6ca-42b8-9659-15b4f280ee3c.sketch_text.stroke-164"),sQuery(id+"F0.wireOp",EDGE,"46c11c21-c6ca-42b8-9659-15b4f280ee3c.sketch_text.stroke-165"),sQuery(id+"F0.wireOp",EDGE,"46c11c21-c6ca-42b8-9659-15b4f280ee3c.sketch_text.stroke-166"),sQuery(id+"F0.wireOp",EDGE,"46c11c21-c6ca-42b8-9659-15b4f280ee3c.sketch_text.stroke-167"),sQuery(id+"F0.wireOp",EDGE,"46c11c21-c6ca-42b8-9659-15b4f280ee3c.sketch_text.stroke-168"),sQuery(id+"F0.wireOp",EDGE,"46c11c21-c6ca-42b8-9659-15b4f280ee3c.sketch_text.stroke-169"),sQuery(id+"F0.wireOp",EDGE,"46c11c21-c6ca-42b8-9659-15b4f280ee3c.sketch_text.stroke-170"),sQuery(id+"F0.wireOp",EDGE,"46c11c21-c6ca-42b8-9659-15b4f280ee3c.sketch_text.stroke-171"),sQuery(id+"F0.wireOp",EDGE,"46c11c21-c6ca-42b8-9659-15b4f280ee3c.sketch_text.stroke-172"),sQuery(id+"F0.wireOp",EDGE,"46c11c21-c6ca-42b8-9659-15b4f280ee3c.sketch_text.stroke-173"),sQuery(id+"F0.wireOp",EDGE,"46c11c21-c6ca-42b8-9659-15b4f280ee3c.sketch_text.stroke-174"),sQuery(id+"F0.wireOp",EDGE,"46c11c21-c6ca-42b8-9659-15b4f280ee3c.sketch_text.stroke-175"),sQuery(id+"F0.wireOp",EDGE,"46c11c21-c6ca-42b8-9659-15b4f280ee3c.sketch_text.stroke-176")])]});
            var Q15;
            Q15=makeQuery(id+"F1.opExtrude","SWEPT_BODY",BODY,{"disambiguationData":[OSD([sQuery(id+"F0.wireOp",EDGE,"46c11c21-c6ca-42b8-9659-15b4f280ee3c.sketch_text.stroke-115"),sQuery(id+"F0.wireOp",EDGE,"46c11c21-c6ca-42b8-9659-15b4f280ee3c.sketch_text.stroke-116"),sQuery(id+"F0.wireOp",EDGE,"46c11c21-c6ca-42b8-9659-15b4f280ee3c.sketch_text.stroke-117"),sQuery(id+"F0.wireOp",EDGE,"46c11c21-c6ca-42b8-9659-15b4f280ee3c.sketch_text.stroke-118"),sQuery(id+"F0.wireOp",EDGE,"46c11c21-c6ca-42b8-9659-15b4f280ee3c.sketch_text.stroke-119"),sQuery(id+"F0.wireOp",EDGE,"46c11c21-c6ca-42b8-9659-15b4f280ee3c.sketch_text.stroke-120"),sQuery(id+"F0.wireOp",EDGE,"46c11c21-c6ca-42b8-9659-15b4f280ee3c.sketch_text.stroke-121"),sQuery(id+"F0.wireOp",EDGE,"46c11c21-c6ca-42b8-9659-15b4f280ee3c.sketch_text.stroke-122"),sQuery(id+"F0.wireOp",EDGE,"46c11c21-c6ca-42b8-9659-15b4f280ee3c.sketch_text.stroke-123"),sQuery(id+"F0.wireOp",EDGE,"46c11c21-c6ca-42b8-9659-15b4f280ee3c.sketch_text.stroke-124"),sQuery(id+"F0.wireOp",EDGE,"46c11c21-c6ca-42b8-9659-15b4f280ee3c.sketch_text.stroke-125"),sQuery(id+"F0.wireOp",EDGE,"46c11c21-c6ca-42b8-9659-15b4f280ee3c.sketch_text.stroke-126"),sQuery(id+"F0.wireOp",EDGE,"46c11c21-c6ca-42b8-9659-15b4f280ee3c.sketch_text.stroke-127"),sQuery(id+"F0.wireOp",EDGE,"46c11c21-c6ca-42b8-9659-15b4f280ee3c.sketch_text.stroke-128"),sQuery(id+"F0.wireOp",EDGE,"46c11c21-c6ca-42b8-9659-15b4f280ee3c.sketch_text.stroke-129"),sQuery(id+"F0.wireOp",EDGE,"46c11c21-c6ca-42b8-9659-15b4f280ee3c.sketch_text.stroke-130"),sQuery(id+"F0.wireOp",EDGE,"46c11c21-c6ca-42b8-9659-15b4f280ee3c.sketch_text.stroke-131"),sQuery(id+"F0.wireOp",EDGE,"46c11c21-c6ca-42b8-9659-15b4f280ee3c.sketch_text.stroke-132"),sQuery(id+"F0.wireOp",EDGE,"46c11c21-c6ca-42b8-9659-15b4f280ee3c.sketch_text.stroke-133")])]});
            var Q16;
            Q16=makeQuery(id+"F1.opExtrude","SWEPT_BODY",BODY,{"disambiguationData":[OSD([sQuery(id+"F0.wireOp",EDGE,"46c11c21-c6ca-42b8-9659-15b4f280ee3c.sketch_text.stroke-185"),sQuery(id+"F0.wireOp",EDGE,"46c11c21-c6ca-42b8-9659-15b4f280ee3c.sketch_text.stroke-186"),sQuery(id+"F0.wireOp",EDGE,"46c11c21-c6ca-42b8-9659-15b4f280ee3c.sketch_text.stroke-187"),sQuery(id+"F0.wireOp",EDGE,"46c11c21-c6ca-42b8-9659-15b4f280ee3c.sketch_text.stroke-188"),sQuery(id+"F0.wireOp",EDGE,"46c11c21-c6ca-42b8-9659-15b4f280ee3c.sketch_text.stroke-189"),sQuery(id+"F0.wireOp",EDGE,"46c11c21-c6ca-42b8-9659-15b4f280ee3c.sketch_text.stroke-190"),sQuery(id+"F0.wireOp",EDGE,"46c11c21-c6ca-42b8-9659-15b4f280ee3c.sketch_text.stroke-191"),sQuery(id+"F0.wireOp",EDGE,"46c11c21-c6ca-42b8-9659-15b4f280ee3c.sketch_text.stroke-192"),sQuery(id+"F0.wireOp",EDGE,"46c11c21-c6ca-42b8-9659-15b4f280ee3c.sketch_text.stroke-193"),sQuery(id+"F0.wireOp",EDGE,"46c11c21-c6ca-42b8-9659-15b4f280ee3c.sketch_text.stroke-194"),sQuery(id+"F0.wireOp",EDGE,"46c11c21-c6ca-42b8-9659-15b4f280ee3c.sketch_text.stroke-195"),sQuery(id+"F0.wireOp",EDGE,"46c11c21-c6ca-42b8-9659-15b4f280ee3c.sketch_text.stroke-196"),sQuery(id+"F0.wireOp",EDGE,"46c11c21-c6ca-42b8-9659-15b4f280ee3c.sketch_text.stroke-197"),sQuery(id+"F0.wireOp",EDGE,"46c11c21-c6ca-42b8-9659-15b4f280ee3c.sketch_text.stroke-198"),sQuery(id+"F0.wireOp",EDGE,"46c11c21-c6ca-42b8-9659-15b4f280ee3c.sketch_text.stroke-199"),sQuery(id+"F0.wireOp",EDGE,"46c11c21-c6ca-42b8-9659-15b4f280ee3c.sketch_text.stroke-200"),sQuery(id+"F0.wireOp",EDGE,"46c11c21-c6ca-42b8-9659-15b4f280ee3c.sketch_text.stroke-201"),sQuery(id+"F0.wireOp",EDGE,"46c11c21-c6ca-42b8-9659-15b4f280ee3c.sketch_text.stroke-202"),sQuery(id+"F0.wireOp",EDGE,"46c11c21-c6ca-42b8-9659-15b4f280ee3c.sketch_text.stroke-203")])]});
            var Q17;
            Q17=makeQuery(id+"F1.opExtrude","SWEPT_BODY",BODY,{"disambiguationData":[OSD([sQuery(id+"F0.wireOp",EDGE,"E46.trimOffspring"),sQuery(id+"F0.wireOp",EDGE,"E48.trimOffspring"),sQuery(id+"F0.wireOp",EDGE,"E51.trimOffspring"),sQuery(id+"F0.wireOp",EDGE,"E53.trimOffspring")])]});
            var Q18;
            Q18=makeQuery(id+"F1.opExtrude","SWEPT_BODY",BODY,{"disambiguationData":[OSD([sQuery(id+"F0.wireOp",EDGE,"E11.right"),sQuery(id+"F0.wireOp",EDGE,"E11.left"),sQuery(id+"F0.wireOp",EDGE,"E11.top"),sQuery(id+"F0.wireOp",EDGE,"E11.bottom"),sQuery(id+"F0.wireOp",EDGE,"E25.filletArc"),sQuery(id+"F0.wireOp",EDGE,"E26.filletArc"),sQuery(id+"F0.wireOp",EDGE,"E27.filletArc"),sQuery(id+"F0.wireOp",EDGE,"E28.filletArc")])]});
            var Q19;
            Q19=makeQuery(id+"F1.opExtrude","SWEPT_BODY",BODY,{"disambiguationData":[OSD([sQuery(id+"F0.wireOp",EDGE,"46c11c21-c6ca-42b8-9659-15b4f280ee3c.sketch_text.stroke-224"),sQuery(id+"F0.wireOp",EDGE,"46c11c21-c6ca-42b8-9659-15b4f280ee3c.sketch_text.stroke-225"),sQuery(id+"F0.wireOp",EDGE,"46c11c21-c6ca-42b8-9659-15b4f280ee3c.sketch_text.stroke-226"),sQuery(id+"F0.wireOp",EDGE,"46c11c21-c6ca-42b8-9659-15b4f280ee3c.sketch_text.stroke-227"),sQuery(id+"F0.wireOp",EDGE,"46c11c21-c6ca-42b8-9659-15b4f280ee3c.sketch_text.stroke-228"),sQuery(id+"F0.wireOp",EDGE,"46c11c21-c6ca-42b8-9659-15b4f280ee3c.sketch_text.stroke-229")])]});
            var Q20;
            Q20=makeQuery(id+"F1.opExtrude","SWEPT_BODY",BODY,{"disambiguationData":[OSD([sQuery(id+"F0.wireOp",EDGE,"46c11c21-c6ca-42b8-9659-15b4f280ee3c.sketch_text.stroke-60"),sQuery(id+"F0.wireOp",EDGE,"46c11c21-c6ca-42b8-9659-15b4f280ee3c.sketch_text.stroke-61"),sQuery(id+"F0.wireOp",EDGE,"46c11c21-c6ca-42b8-9659-15b4f280ee3c.sketch_text.stroke-62"),sQuery(id+"F0.wireOp",EDGE,"46c11c21-c6ca-42b8-9659-15b4f280ee3c.sketch_text.stroke-63"),sQuery(id+"F0.wireOp",EDGE,"46c11c21-c6ca-42b8-9659-15b4f280ee3c.sketch_text.stroke-64"),sQuery(id+"F0.wireOp",EDGE,"46c11c21-c6ca-42b8-9659-15b4f280ee3c.sketch_text.stroke-65"),sQuery(id+"F0.wireOp",EDGE,"46c11c21-c6ca-42b8-9659-15b4f280ee3c.sketch_text.stroke-66"),sQuery(id+"F0.wireOp",EDGE,"46c11c21-c6ca-42b8-9659-15b4f280ee3c.sketch_text.stroke-67"),sQuery(id+"F0.wireOp",EDGE,"46c11c21-c6ca-42b8-9659-15b4f280ee3c.sketch_text.stroke-68"),sQuery(id+"F0.wireOp",EDGE,"46c11c21-c6ca-42b8-9659-15b4f280ee3c.sketch_text.stroke-69"),sQuery(id+"F0.wireOp",EDGE,"46c11c21-c6ca-42b8-9659-15b4f280ee3c.sketch_text.stroke-70"),sQuery(id+"F0.wireOp",EDGE,"46c11c21-c6ca-42b8-9659-15b4f280ee3c.sketch_text.stroke-71"),sQuery(id+"F0.wireOp",EDGE,"46c11c21-c6ca-42b8-9659-15b4f280ee3c.sketch_text.stroke-72"),sQuery(id+"F0.wireOp",EDGE,"46c11c21-c6ca-42b8-9659-15b4f280ee3c.sketch_text.stroke-73"),sQuery(id+"F0.wireOp",EDGE,"46c11c21-c6ca-42b8-9659-15b4f280ee3c.sketch_text.stroke-74"),sQuery(id+"F0.wireOp",EDGE,"46c11c21-c6ca-42b8-9659-15b4f280ee3c.sketch_text.stroke-75"),sQuery(id+"F0.wireOp",EDGE,"46c11c21-c6ca-42b8-9659-15b4f280ee3c.sketch_text.stroke-76"),sQuery(id+"F0.wireOp",EDGE,"46c11c21-c6ca-42b8-9659-15b4f280ee3c.sketch_text.stroke-77"),sQuery(id+"F0.wireOp",EDGE,"46c11c21-c6ca-42b8-9659-15b4f280ee3c.sketch_text.stroke-78")])]});
            var Q21;
            Q21=makeQuery(id+"F1.opExtrude","SWEPT_BODY",BODY,{"disambiguationData":[OSD([sQuery(id+"F0.wireOp",EDGE,"E39"),sQuery(id+"F0.wireOp",EDGE,"E40"),sQuery(id+"F0.wireOp",EDGE,"E44.trimOffspring"),sQuery(id+"F0.wireOp",EDGE,"E52.trimOffspring")])]});
            var Q22;
            Q22=makeQuery(id+"F1.opExtrude","SWEPT_BODY",BODY,{"disambiguationData":[OSD([sQuery(id+"F0.wireOp",EDGE,"46c11c21-c6ca-42b8-9659-15b4f280ee3c.sketch_text.stroke-177"),sQuery(id+"F0.wireOp",EDGE,"46c11c21-c6ca-42b8-9659-15b4f280ee3c.sketch_text.stroke-178"),sQuery(id+"F0.wireOp",EDGE,"46c11c21-c6ca-42b8-9659-15b4f280ee3c.sketch_text.stroke-179"),sQuery(id+"F0.wireOp",EDGE,"46c11c21-c6ca-42b8-9659-15b4f280ee3c.sketch_text.stroke-180"),sQuery(id+"F0.wireOp",EDGE,"46c11c21-c6ca-42b8-9659-15b4f280ee3c.sketch_text.stroke-181"),sQuery(id+"F0.wireOp",EDGE,"46c11c21-c6ca-42b8-9659-15b4f280ee3c.sketch_text.stroke-182"),sQuery(id+"F0.wireOp",EDGE,"46c11c21-c6ca-42b8-9659-15b4f280ee3c.sketch_text.stroke-183"),sQuery(id+"F0.wireOp",EDGE,"46c11c21-c6ca-42b8-9659-15b4f280ee3c.sketch_text.stroke-184")])]});
            var Q23;
            Q23=makeQuery(id+"F1.opExtrude","SWEPT_BODY",BODY,{"disambiguationData":[OSD([sQuery(id+"F0.wireOp",EDGE,"46c11c21-c6ca-42b8-9659-15b4f280ee3c.sketch_text.stroke-0"),sQuery(id+"F0.wireOp",EDGE,"46c11c21-c6ca-42b8-9659-15b4f280ee3c.sketch_text.stroke-1"),sQuery(id+"F0.wireOp",EDGE,"46c11c21-c6ca-42b8-9659-15b4f280ee3c.sketch_text.stroke-2"),sQuery(id+"F0.wireOp",EDGE,"46c11c21-c6ca-42b8-9659-15b4f280ee3c.sketch_text.stroke-3"),sQuery(id+"F0.wireOp",EDGE,"46c11c21-c6ca-42b8-9659-15b4f280ee3c.sketch_text.stroke-4"),sQuery(id+"F0.wireOp",EDGE,"46c11c21-c6ca-42b8-9659-15b4f280ee3c.sketch_text.stroke-5"),sQuery(id+"F0.wireOp",EDGE,"46c11c21-c6ca-42b8-9659-15b4f280ee3c.sketch_text.stroke-6"),sQuery(id+"F0.wireOp",EDGE,"46c11c21-c6ca-42b8-9659-15b4f280ee3c.sketch_text.stroke-7"),sQuery(id+"F0.wireOp",EDGE,"46c11c21-c6ca-42b8-9659-15b4f280ee3c.sketch_text.stroke-8"),sQuery(id+"F0.wireOp",EDGE,"46c11c21-c6ca-42b8-9659-15b4f280ee3c.sketch_text.stroke-9"),sQuery(id+"F0.wireOp",EDGE,"46c11c21-c6ca-42b8-9659-15b4f280ee3c.sketch_text.stroke-10"),sQuery(id+"F0.wireOp",EDGE,"46c11c21-c6ca-42b8-9659-15b4f280ee3c.sketch_text.stroke-11"),sQuery(id+"F0.wireOp",EDGE,"46c11c21-c6ca-42b8-9659-15b4f280ee3c.sketch_text.stroke-12"),sQuery(id+"F0.wireOp",EDGE,"46c11c21-c6ca-42b8-9659-15b4f280ee3c.sketch_text.stroke-13"),sQuery(id+"F0.wireOp",EDGE,"46c11c21-c6ca-42b8-9659-15b4f280ee3c.sketch_text.stroke-14")])]});
            var Q24;
            Q24=makeQuery(id+"F1.opExtrude","SWEPT_BODY",BODY,{"disambiguationData":[OSD([sQuery(id+"F0.wireOp",EDGE,"46c11c21-c6ca-42b8-9659-15b4f280ee3c.sketch_text.stroke-48"),sQuery(id+"F0.wireOp",EDGE,"46c11c21-c6ca-42b8-9659-15b4f280ee3c.sketch_text.stroke-49"),sQuery(id+"F0.wireOp",EDGE,"46c11c21-c6ca-42b8-9659-15b4f280ee3c.sketch_text.stroke-50"),sQuery(id+"F0.wireOp",EDGE,"46c11c21-c6ca-42b8-9659-15b4f280ee3c.sketch_text.stroke-51"),sQuery(id+"F0.wireOp",EDGE,"46c11c21-c6ca-42b8-9659-15b4f280ee3c.sketch_text.stroke-52"),sQuery(id+"F0.wireOp",EDGE,"46c11c21-c6ca-42b8-9659-15b4f280ee3c.sketch_text.stroke-53"),sQuery(id+"F0.wireOp",EDGE,"46c11c21-c6ca-42b8-9659-15b4f280ee3c.sketch_text.stroke-54"),sQuery(id+"F0.wireOp",EDGE,"46c11c21-c6ca-42b8-9659-15b4f280ee3c.sketch_text.stroke-55"),sQuery(id+"F0.wireOp",EDGE,"46c11c21-c6ca-42b8-9659-15b4f280ee3c.sketch_text.stroke-56"),sQuery(id+"F0.wireOp",EDGE,"46c11c21-c6ca-42b8-9659-15b4f280ee3c.sketch_text.stroke-57"),sQuery(id+"F0.wireOp",EDGE,"46c11c21-c6ca-42b8-9659-15b4f280ee3c.sketch_text.stroke-58"),sQuery(id+"F0.wireOp",EDGE,"46c11c21-c6ca-42b8-9659-15b4f280ee3c.sketch_text.stroke-59")])]});
            var Q25;
            Q25=makeQuery(id+"F1.opExtrude","SWEPT_BODY",BODY,{"disambiguationData":[OSD([sQuery(id+"F0.wireOp",EDGE,"46c11c21-c6ca-42b8-9659-15b4f280ee3c.sketch_text.stroke-93"),sQuery(id+"F0.wireOp",EDGE,"46c11c21-c6ca-42b8-9659-15b4f280ee3c.sketch_text.stroke-94"),sQuery(id+"F0.wireOp",EDGE,"46c11c21-c6ca-42b8-9659-15b4f280ee3c.sketch_text.stroke-95"),sQuery(id+"F0.wireOp",EDGE,"46c11c21-c6ca-42b8-9659-15b4f280ee3c.sketch_text.stroke-96"),sQuery(id+"F0.wireOp",EDGE,"46c11c21-c6ca-42b8-9659-15b4f280ee3c.sketch_text.stroke-97"),sQuery(id+"F0.wireOp",EDGE,"46c11c21-c6ca-42b8-9659-15b4f280ee3c.sketch_text.stroke-98"),sQuery(id+"F0.wireOp",EDGE,"46c11c21-c6ca-42b8-9659-15b4f280ee3c.sketch_text.stroke-99"),sQuery(id+"F0.wireOp",EDGE,"46c11c21-c6ca-42b8-9659-15b4f280ee3c.sketch_text.stroke-100")])]});
            var Q26;
            Q26=makeQuery(id+"F1.opExtrude","SWEPT_BODY",BODY,{"disambiguationData":[OSD([sQuery(id+"F0.wireOp",EDGE,"E1.bottom"),sQuery(id+"F0.wireOp",EDGE,"E1.top"),sQuery(id+"F0.wireOp",EDGE,"E1.left"),sQuery(id+"F0.wireOp",EDGE,"E1.right"),sQuery(id+"F0.wireOp",EDGE,"E13.filletArc"),sQuery(id+"F0.wireOp",EDGE,"E14.filletArc"),sQuery(id+"F0.wireOp",EDGE,"E15.filletArc"),sQuery(id+"F0.wireOp",EDGE,"E16.filletArc")])]});
            var Q27;
            Q27=makeQuery(id+"F1.opExtrude","SWEPT_BODY",BODY,{"disambiguationData":[OSD([sQuery(id+"F0.wireOp",EDGE,"E45"),sQuery(id+"F0.wireOp",EDGE,"E47"),sQuery(id+"F0.wireOp",EDGE,"E49.trimOffspring"),sQuery(id+"F0.wireOp",EDGE,"E50.trimOffspring")])]});
            var Q28;
            Q28=qCreatedBy(makeId("Origin.pointOp"),VERTEX);
            transform(context, id + "F2", {"entities" : qUnion([Q0, Q1, Q2, Q3, Q4, Q5, Q6, Q7, Q8, Q9, Q10, Q11, Q12, Q13, Q14, Q15, Q16, Q17, Q18, Q19, Q20, Q21, Q22, Q23, Q24, Q25, Q26, Q27]), "transformType" : TransformType.SCALE_UNIFORMLY, "scale" : .25, "makeCopy" : false, "scalePoint" : qUnion([Q28])});
        }
        {
            var Q0;
            Q0=qCreatedBy(makeId("Top.planeOp"),FACE);
            var sketch = newSketch(context, id + "F3", { "sketchPlane" : qUnion([Q0])});
            skText(sketch, "E55", { "text": "C O R E   D E V I C E\nC O N T R O L L E R", "fontName": "Arimo-Bold.ttf"});
            const initialGuessF3  = {"E55": [-0.02025, -0.003, 1, 0, 0.002]};
            skSetInitialGuess(sketch, initialGuessF3);
            skSolve(sketch);
        }
        {
            var Q0;
            Q0=makeQuery(id+"F3.imprint","IMPRINT",FACE,{"disambiguationData":[TD([[makeQuery(id+"F3.imprint","IMPRINT",EDGE,{"derivedFrom":sQuery(id+"F3.wireOp",EDGE,"E55.sketch_text.stroke-0")}),-1.0]])]});
            var Q1;
            Q1=makeQuery(id+"F3.imprint","IMPRINT",FACE,{"disambiguationData":[TD([[makeQuery(id+"F3.imprint","IMPRINT",EDGE,{"derivedFrom":sQuery(id+"F3.wireOp",EDGE,"E55.sketch_text.stroke-52")}),-1.0]])]});
            var Q2;
            Q2=makeQuery(id+"F3.imprint","IMPRINT",FACE,{"disambiguationData":[TD([[makeQuery(id+"F3.imprint","IMPRINT",EDGE,{"derivedFrom":sQuery(id+"F3.wireOp",EDGE,"E55.sketch_text.stroke-91")}),-1.0]])]});
            var Q3;
            Q3=makeQuery(id+"F3.imprint","IMPRINT",FACE,{"disambiguationData":[TD([[makeQuery(id+"F3.imprint","IMPRINT",EDGE,{"derivedFrom":sQuery(id+"F3.wireOp",EDGE,"E55.sketch_text.stroke-101")}),-1.0]])]});
            var Q4;
            Q4=makeQuery(id+"F3.imprint","IMPRINT",FACE,{"disambiguationData":[TD([[makeQuery(id+"F3.imprint","IMPRINT",EDGE,{"derivedFrom":sQuery(id+"F3.wireOp",EDGE,"E55.sketch_text.stroke-105")}),-1.0]])]});
            var Q5;
            Q5=makeQuery(id+"F3.imprint","IMPRINT",FACE,{"disambiguationData":[TD([[makeQuery(id+"F3.imprint","IMPRINT",EDGE,{"derivedFrom":sQuery(id+"F3.wireOp",EDGE,"E55.sketch_text.stroke-134")}),-1.0]])]});
            var Q6;
            Q6=makeQuery(id+"F3.imprint","IMPRINT",FACE,{"disambiguationData":[TD([[makeQuery(id+"F3.imprint","IMPRINT",EDGE,{"derivedFrom":sQuery(id+"F3.wireOp",EDGE,"E55.sketch_text.stroke-168")}),-1.0]])]});
            var Q7;
            Q7=makeQuery(id+"F3.imprint","IMPRINT",FACE,{"disambiguationData":[TD([[makeQuery(id+"F3.imprint","IMPRINT",EDGE,{"derivedFrom":sQuery(id+"F3.wireOp",EDGE,"E55.sketch_text.stroke-180")}),-1.0]])]});
            var Q8;
            Q8=makeQuery(id+"F3.imprint","IMPRINT",FACE,{"disambiguationData":[TD([[makeQuery(id+"F3.imprint","IMPRINT",EDGE,{"derivedFrom":sQuery(id+"F3.wireOp",EDGE,"E55.sketch_text.stroke-223")}),-1.0]])]});
            var Q9;
            Q9=makeQuery(id+"F3.imprint","IMPRINT",FACE,{"disambiguationData":[TD([[makeQuery(id+"F3.imprint","IMPRINT",EDGE,{"derivedFrom":sQuery(id+"F3.wireOp",EDGE,"E55.sketch_text.stroke-229")}),-1.0]])]});
            var Q10;
            Q10=makeQuery(id+"F3.imprint","IMPRINT",FACE,{"disambiguationData":[TD([[makeQuery(id+"F3.imprint","IMPRINT",EDGE,{"derivedFrom":sQuery(id+"F3.wireOp",EDGE,"E55.sketch_text.stroke-235")}),-1.0]])]});
            var Q11;
            Q11=makeQuery(id+"F3.imprint","IMPRINT",FACE,{"disambiguationData":[TD([[makeQuery(id+"F3.imprint","IMPRINT",EDGE,{"derivedFrom":sQuery(id+"F3.wireOp",EDGE,"E55.sketch_text.stroke-17")}),-1.0]])]});
            var Q12;
            Q12=makeQuery(id+"F3.imprint","IMPRINT",FACE,{"disambiguationData":[TD([[makeQuery(id+"F3.imprint","IMPRINT",EDGE,{"derivedFrom":sQuery(id+"F3.wireOp",EDGE,"E55.sketch_text.stroke-34")}),-1.0]])]});
            var Q13;
            Q13=makeQuery(id+"F3.imprint","IMPRINT",FACE,{"disambiguationData":[TD([[makeQuery(id+"F3.imprint","IMPRINT",EDGE,{"derivedFrom":sQuery(id+"F3.wireOp",EDGE,"E55.sketch_text.stroke-64")}),-1.0]])]});
            var Q14;
            Q14=makeQuery(id+"F3.imprint","IMPRINT",FACE,{"disambiguationData":[TD([[makeQuery(id+"F3.imprint","IMPRINT",EDGE,{"derivedFrom":sQuery(id+"F3.wireOp",EDGE,"E55.sketch_text.stroke-151")}),-1.0]])]});
            var Q15;
            Q15=makeQuery(id+"F3.imprint","IMPRINT",FACE,{"disambiguationData":[TD([[makeQuery(id+"F3.imprint","IMPRINT",EDGE,{"derivedFrom":sQuery(id+"F3.wireOp",EDGE,"E55.sketch_text.stroke-188")}),-1.0]])]});
            var Q16;
            Q16=makeQuery(id+"F3.imprint","IMPRINT",FACE,{"disambiguationData":[TD([[makeQuery(id+"F3.imprint","IMPRINT",EDGE,{"derivedFrom":sQuery(id+"F3.wireOp",EDGE,"E55.sketch_text.stroke-206")}),-1.0]])]});
            var Q17;
            Q17=makeQuery(id+"F3.imprint","IMPRINT",FACE,{"disambiguationData":[TD([[makeQuery(id+"F3.imprint","IMPRINT",EDGE,{"derivedFrom":sQuery(id+"F3.wireOp",EDGE,"E55.sketch_text.stroke-247")}),-1.0]])]});
            var Q18;
            Q18=makeQuery(id+"F3.imprint","IMPRINT",FACE,{"disambiguationData":[TD([[makeQuery(id+"F3.imprint","IMPRINT",EDGE,{"derivedFrom":sQuery(id+"F3.wireOp",EDGE,"E55.sketch_text.stroke-122")}),-1.0]])]});
            var Q19;
            Q19=makeQuery(id+"F3.imprint","IMPRINT",FACE,{"disambiguationData":[TD([[makeQuery(id+"F3.imprint","IMPRINT",EDGE,{"derivedFrom":sQuery(id+"F3.wireOp",EDGE,"E55.sketch_text.stroke-79")}),-1.0]])]});
            extrude(context, id + "F4", {"entities" : qUnion([Q0, Q1, Q2, Q3, Q4, Q5, Q6, Q7, Q8, Q9, Q10, Q11, Q12, Q13, Q14, Q15, Q16, Q17, Q18, Q19]), "depth" : .1 * mm});
        }
    });
